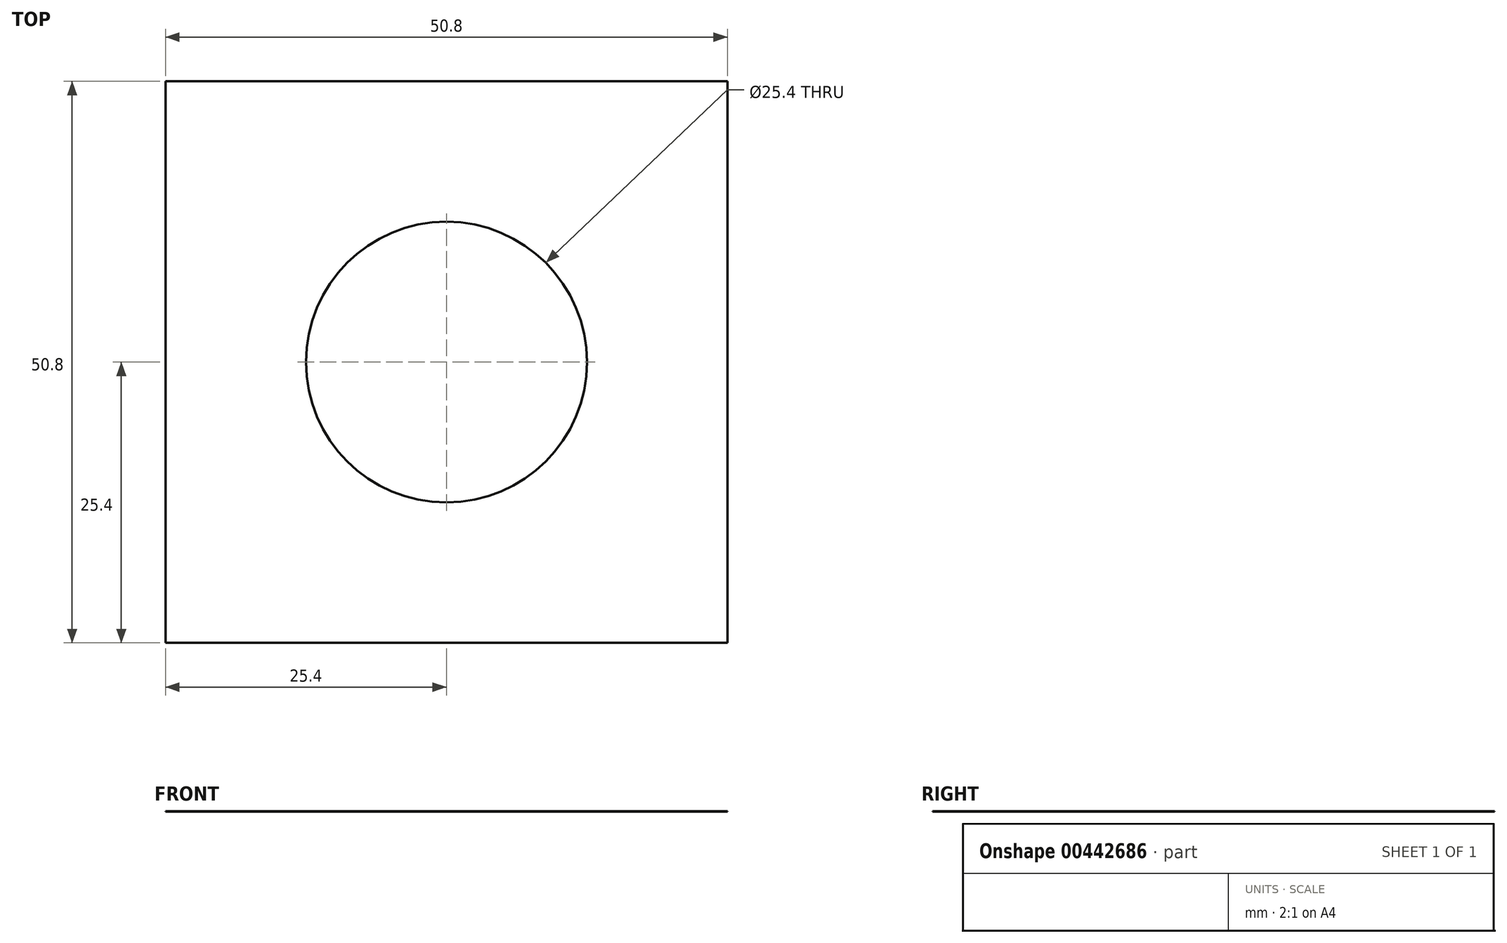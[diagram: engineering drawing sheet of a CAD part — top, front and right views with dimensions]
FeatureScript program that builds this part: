
annotation { "Feature Type Name" : "Feature", "Feature Type Description" : "" }
export const myFeature = defineFeature(function(context is Context, id is Id, definition is map)
    precondition{}
    {
        {
            var Q0;
            Q0=qCreatedBy(makeId("Top.planeOp"),FACE);
            var sketch = newSketch(context, id + "F0", { "sketchPlane" : qUnion([Q0])});
            skLineSegment(sketch, "E0.bottom", {"start": v(-50.8, 25.4) * mm, "end": v(0, 25.4) * mm});
            skLineSegment(sketch, "E0.top", {"start": v(-50.8, -25.4) * mm, "end": v(0, -25.4) * mm});
            skLineSegment(sketch, "E0.left", {"start": v(-50.8, 25.4) * mm, "end": v(-50.8, -25.4) * mm});
            skLineSegment(sketch, "E0.right", {"start": v(0, 25.4) * mm, "end": v(0, -25.4) * mm});
            skPoint(sketch, "E1.centerSnap0", {"position": v(-50.8, 0) * mm});
            skCircle(sketch, "E2", {"center": v(-25.4, 0) * mm, "radius": 12.7 * mm});
            skSolve(sketch);
        }
        {
            var Q0;
            Q0=makeQuery(id+"F0.imprint","IMPRINT",FACE,{"disambiguationData":[TD([[makeQuery(id+"F0.imprint","IMPRINT",EDGE,{"derivedFrom":sQuery(id+"F0.wireOp",EDGE,"E0.bottom")}),-1.0]])]});
            extrude(context, id + "F1", {"entities" : qUnion([Q0]), "depth" : 1 / 203.2 * mm});
        }
    });
